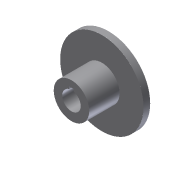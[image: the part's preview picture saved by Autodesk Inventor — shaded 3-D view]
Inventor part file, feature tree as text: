
AUTODESK INVENTOR PART (.ipt)
format: ipt  version: 2011 (Build 150239000, 239)  size: 92,672 bytes
history: native  units: in
note: dims shown in document units (in); Inventor stores cm internally (conversion verified against a paired STEP export)
features: extrude x3, sketch x3
ambient origin geometry x8: Origin, YZ Plane, XZ Plane, XY Plane, X Axis, Y Axis, Z Axis, Center Point
bodies: Solid1 (feature_tree)
feature tree (6):
  extrude  "Extrusion1"  Depth=0.18in TaperAngle=0.0deg
  extrude  "Extrusion2"  Depth=0.82in TaperAngle=0.0deg
  extrude  "Extrusion3"  Depth=0.125in
  sketch  "Sketch1"  dims[d0=2.25in d1=0.18in d2=0.0in]
  sketch  "Sketch2"  dims[d3=0.958in d4=0.82in d5=0.0in]
  sketch  "Sketch3"  dims[d6=0.5in d7=0.125in d8=0.125in d9=0.82in d10=0.0in]
